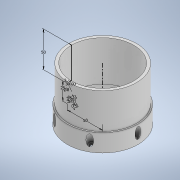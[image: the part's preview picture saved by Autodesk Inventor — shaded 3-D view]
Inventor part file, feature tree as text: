
AUTODESK INVENTOR PART (.ipt)
format: ipt  version: 2022 (Build 260153000, 153)  size: 197,120 bytes
history: native  units: mm
features: revolve x2, sketch x1, pattern_circular x1
ambient origin geometry x8: Origin, YZ Plane, XZ Plane, XY Plane, X Axis, Y Axis, Z Axis, Center Point
bodies: Solid1 (feature_tree)
feature tree (4):
  sketch  "Sketch1"  dims[d0=25.0mm d1=2.0mm d2=50.0mm d3=30.0deg d5=3.0mm d6=2.0mm d7=4.0mm d8=4.0mm d9=8.0mm d10=2.0mm d11=2.0mm d12=4.5mm d13=50.0mm d14=8.0mm d15=90.0deg d16=360.0deg d17=0.5mm d18=60.0mm d19=360.0deg]
  revolve  "Revolution1"  [1 undecoded]
  revolve  "Revolution2"  [1 undecoded]
  pattern_circular  "Circular Pattern1"  Angle=30.0deg  [1 undecoded]
note: 3 required parameter values undecoded (feature->parameter linkage not recoverable at this tier; creation-order binding heuristic only, values carry confidence <= 0.55)